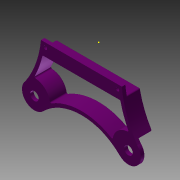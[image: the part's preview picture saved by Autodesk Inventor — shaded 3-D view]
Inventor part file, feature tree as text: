
AUTODESK INVENTOR PART (.ipt)
format: ipt  version: 2015 (Build 190159000, 159)  size: 366,080 bytes
history: native  units: mm
features: sketch x12, extrude x11, fillet x7, projected_geometry x6, plane x1
ambient origin geometry x8: Origin, YZ Plane, XZ Plane, XY Plane, X Axis, Y Axis, Z Axis, Center Point
bodies: Solid1 (feature_tree)
feature tree (37):
  extrude  "Extrusion1"  Depth=3.5mm
  extrude  "Extrusion2"  Depth=3.5mm TaperAngle=0.0deg
  extrude  "Extrusion3"  Depth=3.5mm TaperAngle=0.0deg
  extrude  "Extrusion4"  Depth=13.5mm TaperAngle=0.0deg
  extrude  "Extrusion5"  Depth=13.5mm TaperAngle=0.0deg
  extrude  "Extrusion6"  Depth=13.5mm TaperAngle=0.0deg
  extrude  "Extrusion8"  Depth=3.5mm TaperAngle=0.0deg
  extrude  "Extrusion9"  Depth=4.4125mm
  extrude  "Extrusion10"  TaperAngle=45.0deg  [1 undecoded]
  plane  "Work Plane1"
  extrude  "Extrusion11"  Depth=1.0mm
  fillet  "Fillet4"  Radius=1.0mm
  fillet  "Fillet5"  Radius=1.0mm
  fillet  "Fillet6"  Radius=1.0mm
  fillet  "Fillet7"  Radius=1.0mm
  sketch  "Sketch19"
  fillet  "Fillet8"  Radius=1.0mm
  fillet  "Fillet9"  Radius=1.0mm
  fillet  "Fillet10"  Radius=10.0mm
  extrude  "Extrusion14"  [1 undecoded]
  sketch  "Sketch1"  dims[d13=3.5mm d16=3.5mm]
  sketch  "Sketch2"  dims[d24=90.0deg d25=3.5mm d26=0.0mm]
  sketch  "Sketch3"  dims[d30=8.907301mm d32=3.5mm d33=0.0mm]
  projected_geometry  "Projected Loop1"
  sketch  "Sketch4"  dims[d34=13.5mm d35=0.0mm d38=13.5mm d39=0.0mm]
  sketch  "Sketch5"  dims[d40=31.55mm d41=13.5mm d42=0.0mm]
  projected_geometry  "Projected Loop2"
  sketch  "Sketch7"  dims[d44=3.5mm d45=0.0mm d51=13.5mm d52=0.0mm]
  projected_geometry  "Projected Loop3"
  sketch  "Sketch13"  dims[d53=3.5mm d54=0.0mm d55=3.5mm d56=0.0mm]
  projected_geometry  "Projected Loop5"
  sketch  "Sketch14"  dims[d57=0.0mm d58=4.4125mm]
  projected_geometry  "Projected Loop6"
  sketch  "Sketch15"  dims[d59=90.0deg d60=45.0deg]
  projected_geometry  "Projected Loop7"
  sketch  "Sketch16"  dims[d61=50.0mm d62=0.0mm d67=1.0mm d68=1.0mm d69=1.0mm d70=1.0mm d75=1.0mm d103=1.0mm d104=1.0mm d108=10.0mm d109=0.0mm]
  sketch  "Sketch27"
note: 2 required parameter values undecoded (feature->parameter linkage not recoverable at this tier; creation-order binding heuristic only, values carry confidence <= 0.55)
